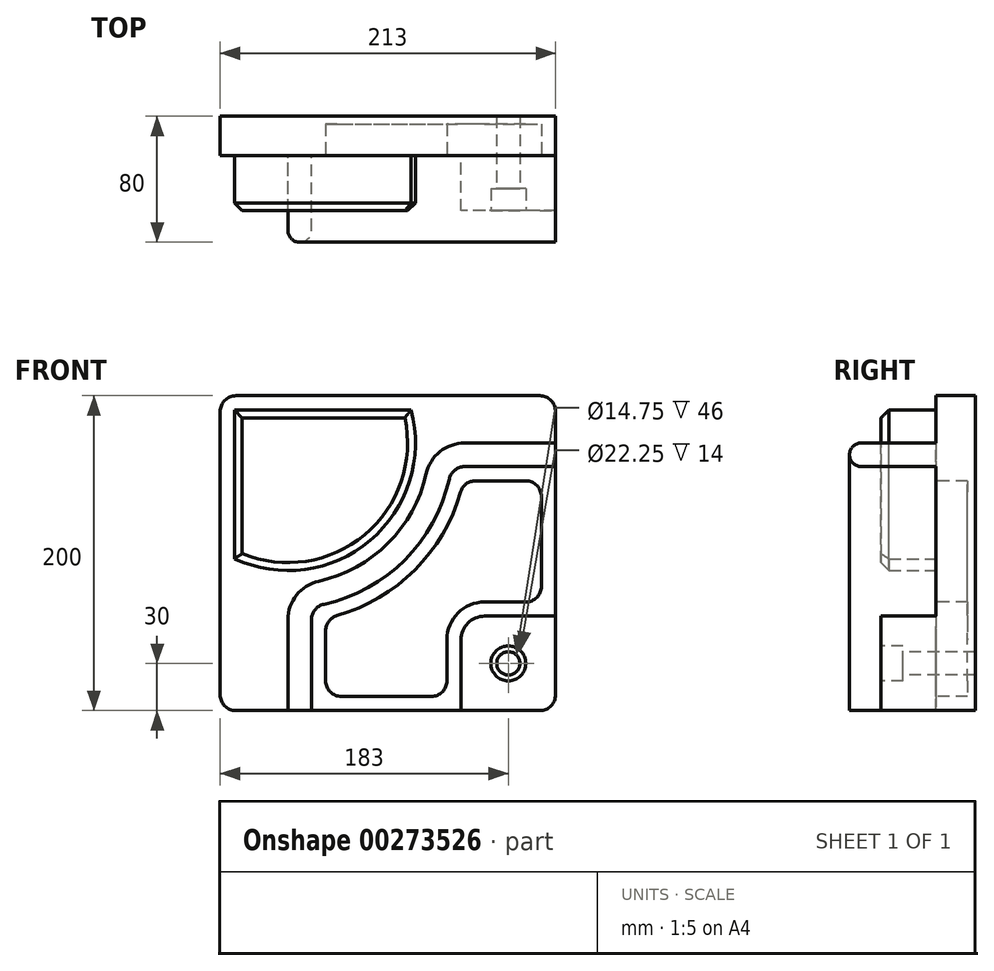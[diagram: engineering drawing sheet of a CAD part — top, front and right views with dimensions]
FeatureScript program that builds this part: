
annotation { "Feature Type Name" : "Feature", "Feature Type Description" : "" }
export const myFeature = defineFeature(function(context is Context, id is Id, definition is map)
    precondition{}
    {
        {
            var Q0;
            Q0=qCreatedBy(makeId("Front.planeOp"),FACE);
            var sketch = newSketch(context, id + "F0", { "sketchPlane" : qUnion([Q0])});
            skLineSegment(sketch, "E0", {"start": v(-96.5, 100) * mm, "end": v(96.5, 100) * mm});
            skLineSegment(sketch, "E1", {"start": v(106.5, 90) * mm, "end": v(106.5, -90) * mm});
            skLineSegment(sketch, "E2", {"start": v(96.5, -100) * mm, "end": v(-96.5, -100) * mm});
            skLineSegment(sketch, "E3", {"start": v(-106.5, 90) * mm, "end": v(-106.5, -90) * mm});
            skPoint(sketch, "E4.visualSharp", {"position": v(-106.5, 100) * mm});
            skArc(sketch, "E4.filletArc", {"start": v(-96.5, 100) * mm, "mid": v(-103.57, 97.07) * mm, "end": v(-106.5, 90) * mm});
            skPoint(sketch, "E5.visualSharp", {"position": v(106.5, 100) * mm});
            skArc(sketch, "E5.filletArc", {"start": v(106.5, 90) * mm, "mid": v(103.57, 97.07) * mm, "end": v(96.5, 100) * mm});
            skPoint(sketch, "E6.visualSharp", {"position": v(106.5, -100) * mm});
            skArc(sketch, "E6.filletArc", {"start": v(96.5, -100) * mm, "mid": v(103.57, -97.07) * mm, "end": v(106.5, -90) * mm});
            skPoint(sketch, "E7.visualSharp", {"position": v(-106.5, -100) * mm});
            skArc(sketch, "E7.filletArc", {"start": v(-106.5, -90) * mm, "mid": v(-103.57, -97.07) * mm, "end": v(-96.5, -100) * mm});
            skPoint(sketch, "E8", {"position": v(76.5, -70) * mm});
            skLineSegment(sketch, "E9", {"start": v(106.5, -40) * mm, "end": v(61.5, -40) * mm});
            skLineSegment(sketch, "E10", {"start": v(46.5, -55) * mm, "end": v(46.5, -100) * mm});
            skPoint(sketch, "E11.visualSharp", {"position": v(46.5, -40) * mm});
            skArc(sketch, "E11.filletArc", {"start": v(61.5, -40) * mm, "mid": v(50.9, -44.4) * mm, "end": v(46.5, -55) * mm});
            skPoint(sketch, "E12", {"position": v(-63.5, 70) * mm});
            skArc(sketch, "E13", {"start": v(-97.5, -3.52) * mm, "mid": v(-11.32, 8.04) * mm, "end": v(14.73, 91) * mm});
            skLineSegment(sketch, "E14", {"start": v(-63.5, -100) * mm, "end": v(-63.5, -42.25) * mm});
            skLineSegment(sketch, "E15", {"start": v(-97.5, 91) * mm, "end": v(14.73, 91) * mm});
            skLineSegment(sketch, "E16", {"start": v(-97.5, 91) * mm, "end": v(-97.5, -3.52) * mm});
            skLineSegment(sketch, "E17", {"start": v(106.5, 70) * mm, "end": v(48.75, 70) * mm});
            skArc(sketch, "E18", {"start": v(-43.93, -17.85) * mm, "mid": v(0.14, 6.36) * mm, "end": v(24.35, 50.43) * mm});
            skPoint(sketch, "E19.visualSharp", {"position": v(26.5, 70) * mm});
            skArc(sketch, "E19.filletArc", {"start": v(48.75, 70) * mm, "mid": v(33.11, 64.5) * mm, "end": v(24.35, 50.43) * mm});
            skPoint(sketch, "E20.visualSharp", {"position": v(-63.5, -20) * mm});
            skArc(sketch, "E20.filletArc", {"start": v(-43.93, -17.85) * mm, "mid": v(-58, -26.61) * mm, "end": v(-63.5, -42.25) * mm});
            skLineSegment(sketch, "E21.0", {"start": v(-48.5, -100) * mm, "end": v(-48.5, -42.25) * mm});
            skLineSegment(sketch, "E21.1", {"start": v(106.5, 55) * mm, "end": v(48.75, 55) * mm});
            skArc(sketch, "E21.2", {"start": v(48.75, 55) * mm, "mid": v(42.5, 52.8) * mm, "end": v(38.99, 47.17) * mm});
            skArc(sketch, "E21.3", {"start": v(-40.67, -32.49) * mm, "mid": v(10.75, -4.25) * mm, "end": v(38.99, 47.17) * mm});
            skArc(sketch, "E21.4", {"start": v(-40.67, -32.49) * mm, "mid": v(-46.3, -36) * mm, "end": v(-48.5, -42.25) * mm});
            skLineSegment(sketch, "E22", {"start": v(-39.5, -81) * mm, "end": v(-39.5, -49.25) * mm});
            skLineSegment(sketch, "E23", {"start": v(87.5, 46) * mm, "end": v(55.75, 46) * mm});
            skLineSegment(sketch, "E24", {"start": v(-29.5, -91) * mm, "end": v(27.5, -91) * mm});
            skLineSegment(sketch, "E25", {"start": v(37.5, -81) * mm, "end": v(37.5, -55) * mm});
            skLineSegment(sketch, "E26", {"start": v(61.5, -31) * mm, "end": v(87.5, -31) * mm});
            skLineSegment(sketch, "E27", {"start": v(97.5, -21) * mm, "end": v(97.5, 36) * mm});
            skArc(sketch, "E28.0", {"start": v(-32.24, -39.63) * mm, "mid": v(17.11, -10.61) * mm, "end": v(46.13, 38.74) * mm});
            skPoint(sketch, "E29.visualSharp", {"position": v(97.5, 46) * mm});
            skArc(sketch, "E29.filletArc", {"start": v(97.5, 36) * mm, "mid": v(94.57, 43.07) * mm, "end": v(87.5, 46) * mm});
            skArc(sketch, "E30.filletArc", {"start": v(55.75, 46) * mm, "mid": v(49.72, 43.98) * mm, "end": v(46.13, 38.74) * mm});
            skArc(sketch, "E31.filletArc", {"start": v(-32.24, -39.63) * mm, "mid": v(-37.48, -43.22) * mm, "end": v(-39.5, -49.25) * mm});
            skPoint(sketch, "E32.visualSharp", {"position": v(-39.5, -91) * mm});
            skArc(sketch, "E32.filletArc", {"start": v(-39.5, -81) * mm, "mid": v(-36.57, -88.07) * mm, "end": v(-29.5, -91) * mm});
            skPoint(sketch, "E33.visualSharp", {"position": v(37.5, -91) * mm});
            skArc(sketch, "E33.filletArc", {"start": v(27.5, -91) * mm, "mid": v(34.57, -88.07) * mm, "end": v(37.5, -81) * mm});
            skPoint(sketch, "E34.visualSharp", {"position": v(97.5, -31) * mm});
            skArc(sketch, "E34.filletArc", {"start": v(87.5, -31) * mm, "mid": v(94.57, -28.07) * mm, "end": v(97.5, -21) * mm});
            skArc(sketch, "E35.0", {"start": v(61.5, -31) * mm, "mid": v(44.53, -38.03) * mm, "end": v(37.5, -55) * mm});
            skSolve(sketch);
        }
        {
            var Q0;
            {var subQ3=sQuery(id+"F0.wireOp",EDGE,"E9");Q0=makeQuery(id+"F0.imprint","IMPRINT",FACE,{"disambiguationData":[TD([[makeQuery(id+"F0.imprint","IMPRINT",EDGE,{"derivedFrom":subQ3}),-1.0]])]});}
            var Q1;
            Q1=makeQuery(id+"F0.imprint","IMPRINT",FACE,{"disambiguationData":[TD([[makeQuery(id+"F0.imprint","IMPRINT",EDGE,{"derivedFrom":sQuery(id+"F0.wireOp",EDGE,"E0")}),-1.0]])]});
            var Q2;
            Q2=makeQuery(id+"F0.imprint","IMPRINT",FACE,{"disambiguationData":[TD([[makeQuery(id+"F0.imprint","IMPRINT",EDGE,{"derivedFrom":sQuery(id+"F0.wireOp",EDGE,"E13")}),1.0]])]});
            var Q3;
            Q3=makeQuery(id+"F0.imprint","IMPRINT",FACE,{"disambiguationData":[TD([[makeQuery(id+"F0.imprint","IMPRINT",EDGE,{"derivedFrom":sQuery(id+"F0.wireOp",EDGE,"E22")}),-1.0]])]});
            var Q4;
            {var subQ0=sQuery(id+"F0.wireOp",EDGE,"E14");Q4=makeQuery(id+"F0.imprint","IMPRINT",FACE,{"disambiguationData":[TD([[makeQuery(id+"F0.imprint","IMPRINT",EDGE,{"derivedFrom":subQ0}),-1.0]])]});}
            var Q5;
            {var subQ1=sQuery(id+"F0.wireOp",EDGE,"E6.filletArc");Q5=makeQuery(id+"F0.imprint","IMPRINT",FACE,{"disambiguationData":[TD([[makeQuery(id+"F0.imprint","IMPRINT",EDGE,{"derivedFrom":subQ1}),1.0]])]});}
            extrude(context, id + "F1", {"entities" : qUnion([Q0, Q1, Q2, Q3, Q4, Q5]), "oppositeDirection" : true, "depth" : 25 * mm});
        }
        {
            var Q0;
            Q0=makeQuery(id+"F0.imprint","IMPRINT",FACE,{"disambiguationData":[TD([[makeQuery(id+"F0.imprint","IMPRINT",EDGE,{"derivedFrom":sQuery(id+"F0.wireOp",EDGE,"E13")}),1.0]])]});
            var Q1;
            {var subQ1=sQuery(id+"F0.wireOp",EDGE,"E6.filletArc");Q1=makeQuery(id+"F0.imprint","IMPRINT",FACE,{"disambiguationData":[TD([[makeQuery(id+"F0.imprint","IMPRINT",EDGE,{"derivedFrom":subQ1}),1.0]])]});}
            extrude(context, id + "F2", {"entities" : qUnion([Q0, Q1]), "operationType" : NewBodyOperationType.ADD, "depth" : 35 * mm});
        }
        {
            var Q0;
            {var subQ0=sQuery(id+"F0.wireOp",EDGE,"E14");Q0=makeQuery(id+"F0.imprint","IMPRINT",FACE,{"disambiguationData":[TD([[makeQuery(id+"F0.imprint","IMPRINT",EDGE,{"derivedFrom":subQ0}),-1.0]])]});}
            extrude(context, id + "F3", {"entities" : qUnion([Q0]), "operationType" : NewBodyOperationType.ADD, "depth" : 55 * mm});
        }
        {
            var Q0;
            Q0=makeQuery(id+"F0.imprint","IMPRINT",FACE,{"disambiguationData":[TD([[makeQuery(id+"F0.imprint","IMPRINT",EDGE,{"derivedFrom":sQuery(id+"F0.wireOp",EDGE,"E22")}),-1.0]])]});
            extrude(context, id + "F4", {"entities" : qUnion([Q0]), "operationType" : NewBodyOperationType.REMOVE, "oppositeDirection" : true, "depth" : 20 * mm});
        }
        {
            var Q0;
            Q0=makeQuery(id+"F2.opExtrude","CAP_EDGE",EDGE,{"disambiguationData":[OSD([sQuery(id+"F0.wireOp",EDGE,"E13")])],"isStart":false});
            var Q1;
            Q1=makeQuery(id+"F2.opExtrude","CAP_EDGE",EDGE,{"disambiguationData":[OSD([sQuery(id+"F0.wireOp",EDGE,"E15")])],"isStart":false});
            var Q2;
            Q2=makeQuery(id+"F2.opExtrude","CAP_EDGE",EDGE,{"disambiguationData":[OSD([sQuery(id+"F0.wireOp",EDGE,"E16")])],"isStart":false});
            chamfer(context, id + "F5", {"entities" : qUnion([Q0, Q1, Q2]), "chamferType" : ChamferType.OFFSET_ANGLE, "width" : 5 * mm, "oppositeDirection" : false, "angle" : 45 * degree, "tangentPropagation" : true});
        }
        {
            var Q0;
            Q0=makeQuery(id+"F2.opExtrude","CAP_FACE",FACE,{"disambiguationData":[OSD([sQuery(id+"F0.wireOp",EDGE,"E1"),sQuery(id+"F0.wireOp",EDGE,"E2"),sQuery(id+"F0.wireOp",EDGE,"E6.filletArc"),sQuery(id+"F0.wireOp",EDGE,"E9"),sQuery(id+"F0.wireOp",EDGE,"E10"),sQuery(id+"F0.wireOp",EDGE,"E11.filletArc")])],"isStart":false});
            var sketch = newSketch(context, id + "F6", { "sketchPlane" : qUnion([Q0])});
            skArc(sketch, "E36.0.0", {"start": v(61.5, -40) * mm, "mid": v(50.9, -44.4) * mm, "end": v(46.5, -55) * mm});
            skLineSegment(sketch, "E36.0.1", {"start": v(46.5, -55) * mm, "end": v(46.5, -100) * mm});
            skLineSegment(sketch, "E36.0.2", {"start": v(46.5, -100) * mm, "end": v(96.5, -100) * mm});
            skArc(sketch, "E36.0.3", {"start": v(96.5, -100) * mm, "mid": v(103.57, -97.07) * mm, "end": v(106.5, -90) * mm});
            skLineSegment(sketch, "E36.0.4", {"start": v(106.5, -90) * mm, "end": v(106.5, -40) * mm});
            skLineSegment(sketch, "E36.0.5", {"start": v(106.5, -40) * mm, "end": v(61.5, -40) * mm});
            skPoint(sketch, "E37", {"position": v(76.5, -70) * mm});
            skSolve(sketch);
        }
        {
            var Q0;
            Q0=sQuery(id+"F6.wireOp",VERTEX,"E37");
            var Q1;
            Q1=makeQuery(id+"F1.opExtrude","SWEPT_BODY",BODY,{"disambiguationData":[OSD([sQuery(id+"F0.wireOp",EDGE,"E0"),sQuery(id+"F0.wireOp",EDGE,"E1"),sQuery(id+"F0.wireOp",EDGE,"E2"),sQuery(id+"F0.wireOp",EDGE,"E3"),sQuery(id+"F0.wireOp",EDGE,"E4.filletArc"),sQuery(id+"F0.wireOp",EDGE,"E5.filletArc"),sQuery(id+"F0.wireOp",EDGE,"E6.filletArc"),sQuery(id+"F0.wireOp",EDGE,"E7.filletArc")])]});
            hole(context, id + "F7", {"style" : HoleStyle.C_BORE, "endStyle" : HoleEndStyle.THROUGH, "standardTappedOrClearance" : lookupTablePath({ "standard" : "ISO", "fit" : "Close", "size" : "M14", "type" : "Clearance" }), "standardBlindInLast" : lookupTablePath({ "fit" : "Close", "standard" : "ISO", "size" : "M14", "type" : "Clearance" }), "holeDiameter" : 14.75 * mm, "cBoreDiameter" : 22.25 * mm, "cBoreDepth" : 14 * mm, "tappedDepth" : 12 * mm, "tapClearance" : 3, "locations" : qUnion([Q0]), "scope" : qUnion([Q1])});
        }
        {
            var Q0;
            Q0=makeQuery(id+"F3.opExtrude","CAP_EDGE",EDGE,{"disambiguationData":[OSD([sQuery(id+"F0.wireOp",EDGE,"E21.0")])],"isStart":false});
            var Q1;
            Q1=makeQuery(id+"F3.opExtrude","CAP_EDGE",EDGE,{"disambiguationData":[OSD([sQuery(id+"F0.wireOp",EDGE,"E14")])],"isStart":false});
            fillet(context, id + "F8", {"entities" : qUnion([Q0, Q1]), "radius" : 7.48 * mm, "tangentPropagation" : true, "allowEdgeOverflow" : false});
        }
    });
